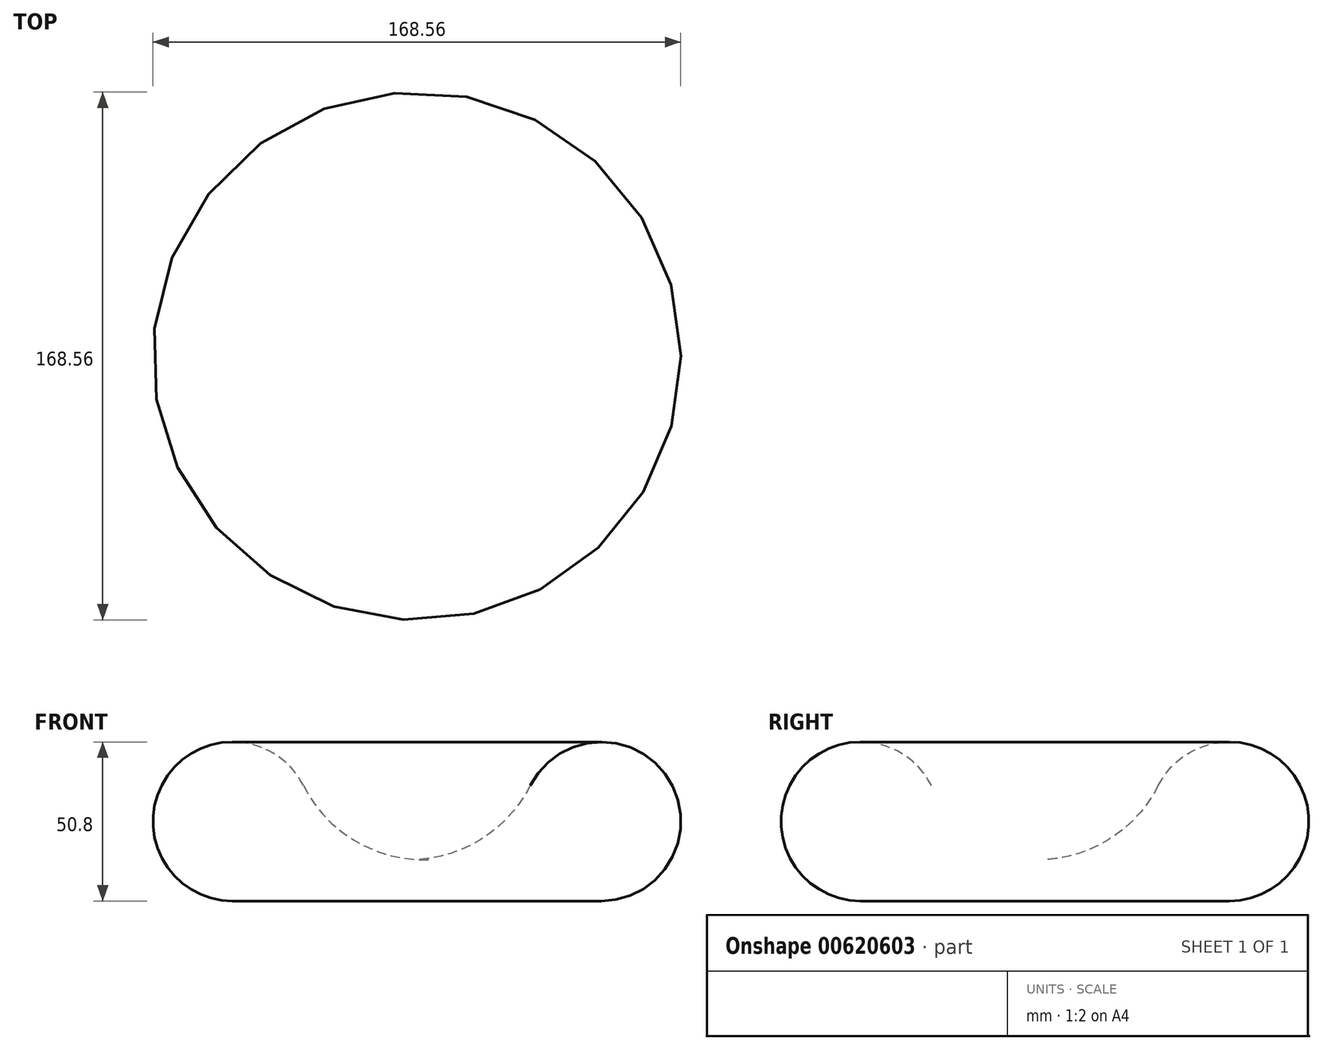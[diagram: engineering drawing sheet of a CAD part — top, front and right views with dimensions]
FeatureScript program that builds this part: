
annotation { "Feature Type Name" : "Feature", "Feature Type Description" : "" }
export const myFeature = defineFeature(function(context is Context, id is Id, definition is map)
    precondition{}
    {
        {
            var Q0;
            Q0=qCreatedBy(makeId("Front.planeOp"),FACE);
            var sketch = newSketch(context, id + "F0", { "sketchPlane" : qUnion([Q0])});
            skArc(sketch, "E0", {"start": v(-57.19, 29.73) * mm, "mid": v(-101.49, 31.55) * mm, "end": v(-79.84, -7.15) * mm});
            skArc(sketch, "E1", {"start": v(-57.19, 29.73) * mm, "mid": v(-42.24, 13.05) * mm, "end": v(-20.96, 6.08) * mm});
            skLineSegment(sketch, "E2", {"start": v(-20.96, 6.08) * mm, "end": v(-20.96, -7.15) * mm});
            skLineSegment(sketch, "E3", {"start": v(-20.96, -7.15) * mm, "end": v(-79.84, -7.15) * mm});
            skSolve(sketch);
        }
        {
            var Q0;
            Q0=makeQuery(id+"F0.imprint","IMPRINT",FACE,{"disambiguationData":[TD([[makeQuery(id+"F0.imprint","IMPRINT",EDGE,{"derivedFrom":sQuery(id+"F0.wireOp",EDGE,"E0")}),1.0]])]});
            var Q1;
            Q1=sQuery(id+"F0.wireOp",EDGE,"E2");
            revolve(context, id + "F1", {"entities" : qUnion([Q0]), "axis" : qUnion([Q1]), "revolveType" : RevolveType.FULL});
        }
    });
